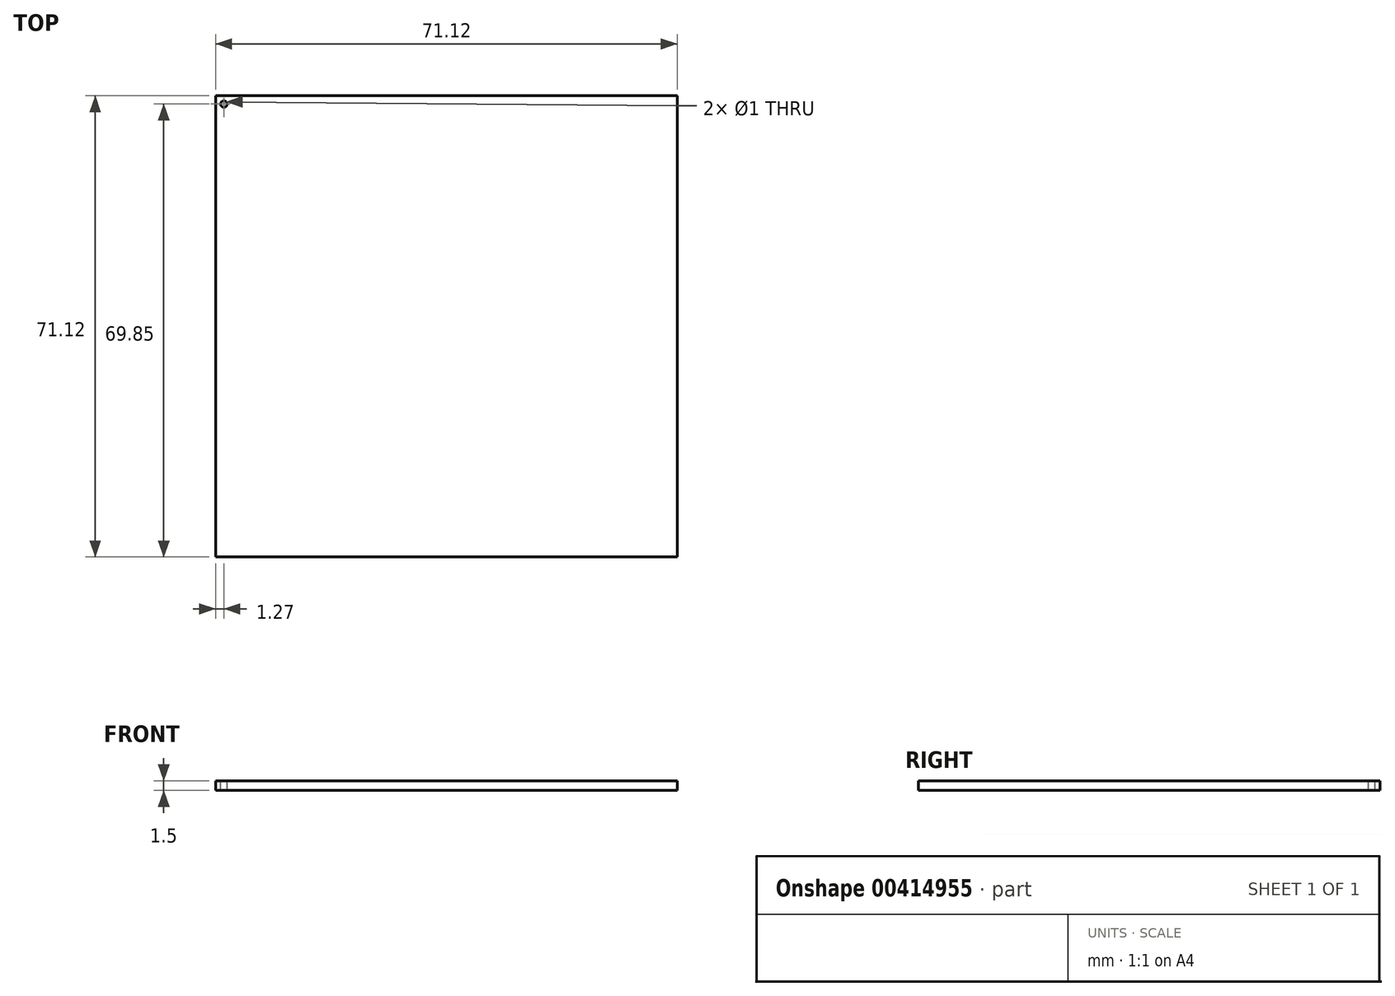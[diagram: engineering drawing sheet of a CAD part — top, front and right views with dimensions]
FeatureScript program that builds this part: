
annotation { "Feature Type Name" : "Feature", "Feature Type Description" : "" }
export const myFeature = defineFeature(function(context is Context, id is Id, definition is map)
    precondition{}
    {
        {
            var Q0;
            Q0=qCreatedBy(makeId("Top.planeOp"),FACE);
            var sketch = newSketch(context, id + "F0", { "sketchPlane" : qUnion([Q0])});
            skLineSegment(sketch, "E0.bottom", {"start": v(35.56, 35.56) * mm, "end": v(-35.56, 35.56) * mm});
            skLineSegment(sketch, "E0.top", {"start": v(35.56, -35.56) * mm, "end": v(-35.56, -35.56) * mm});
            skLineSegment(sketch, "E0.left", {"start": v(35.56, 35.56) * mm, "end": v(35.56, -35.56) * mm});
            skLineSegment(sketch, "E0.right", {"start": v(-35.56, 35.56) * mm, "end": v(-35.56, -35.56) * mm});
            skPoint(sketch, "E0.middle", {"position": v(0, 0) * mm});
            skSolve(sketch);
        }
        {
            var Q0;
            Q0 = qSketchRegion(id + "F0", true);
            extrude(context, id + "F1", {"entities" : qUnion([Q0]), "depth" : 1.5 * mm});
        }
        {
            var Q0;
            Q0=makeQuery(id+"F1.opExtrude","CAP_FACE",FACE,{"disambiguationData":[OSD([sQuery(id+"F0.wireOp",EDGE,"E0.bottom"),sQuery(id+"F0.wireOp",EDGE,"E0.top"),sQuery(id+"F0.wireOp",EDGE,"E0.left"),sQuery(id+"F0.wireOp",EDGE,"E0.right")])],"isStart":false});
            var sketch = newSketch(context, id + "F2", { "sketchPlane" : qUnion([Q0])});
            skCircle(sketch, "E1", {"center": v(-34.29, 34.29) * mm, "radius": 0.5 * mm});
            skSolve(sketch);
        }
        {
            var Q0;
            Q0=sQuery(id+"F2.wireOp",VERTEX,"E1.center");
            var Q1;
            Q1=makeQuery(id+"F1.opExtrude","SWEPT_BODY",BODY,{"disambiguationData":[OSD([sQuery(id+"F0.wireOp",EDGE,"E0.bottom"),sQuery(id+"F0.wireOp",EDGE,"E0.top"),sQuery(id+"F0.wireOp",EDGE,"E0.left"),sQuery(id+"F0.wireOp",EDGE,"E0.right")])]});
            hole(context, id + "F3", {"style" : HoleStyle.SIMPLE, "endStyle" : HoleEndStyle.THROUGH, "holeDiameter" : 1 * mm, "isTappedThrough" : true, "tappedDepth" : 12 * mm, "tapClearance" : 3, "locations" : qUnion([Q0]), "scope" : qUnion([Q1])});
        }
    });
